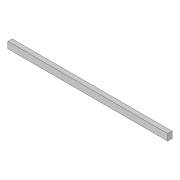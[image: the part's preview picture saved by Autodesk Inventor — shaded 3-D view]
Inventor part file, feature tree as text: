
AUTODESK INVENTOR PART (.ipt)
format: ipt  version: 2018 (Build 220112000, 112)  size: 74,752 bytes
history: native  units: in
note: dims shown in document units (in); Inventor stores cm internally (conversion verified against a paired STEP export)
features: extrude x1, sketch x1
ambient origin geometry x8: Origin, YZ Plane, XZ Plane, XY Plane, X Axis, Y Axis, Z Axis, Center Point
bodies: Solid1 (feature_tree)
feature tree (2):
  extrude  "Extrusion1"  TaperAngle=90.0deg  [1 undecoded]
  sketch  "Sketch1"  dims[d0=0.2953in d1=90.0deg d2=7.2835in d3=90.0deg d4=0.2953in d5=90.0deg d6=0.1969in d7=0.0in]
note: 1 required parameter value undecoded (feature->parameter linkage not recoverable at this tier; creation-order binding heuristic only, values carry confidence <= 0.55)
